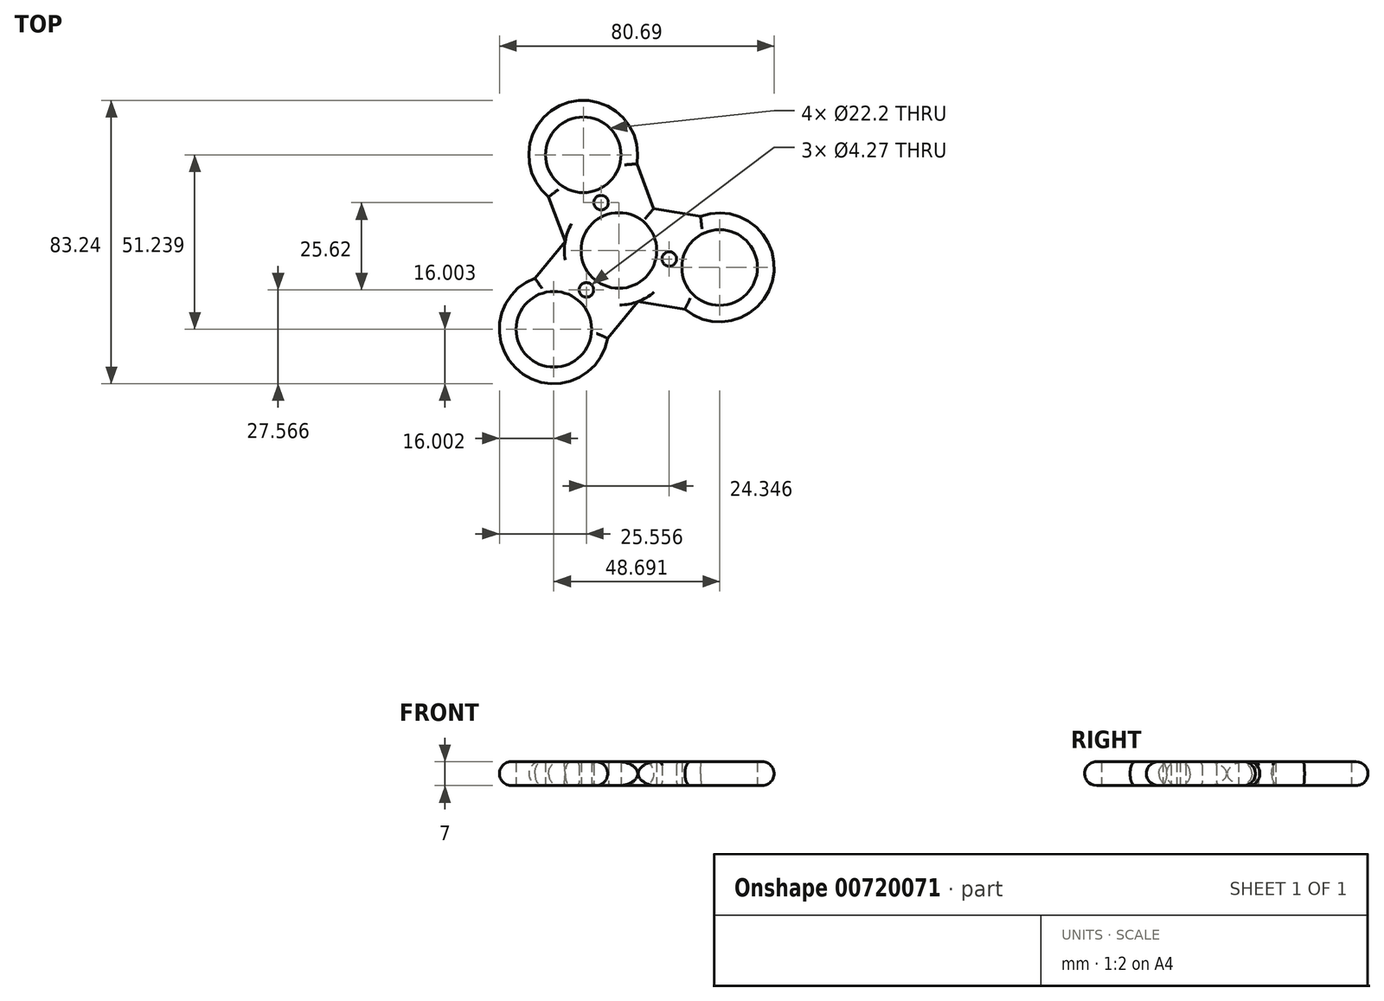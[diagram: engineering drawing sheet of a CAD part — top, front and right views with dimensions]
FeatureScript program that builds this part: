
annotation { "Feature Type Name" : "Feature", "Feature Type Description" : "" }
export const myFeature = defineFeature(function(context is Context, id is Id, definition is map)
    precondition{}
    {
        {
            var Q0;
            Q0=qCreatedBy(makeId("Top.planeOp"),FACE);
            var sketch = newSketch(context, id + "F0", { "sketchPlane" : qUnion([Q0])});
            skCircle(sketch, "E0", {"center": v(0, 0) * mm, "radius": 11.1 * mm});
            skLineSegment(sketch, "E1", {"start": v(0, 0) * mm, "end": v(-10.47, 28.11) * mm});
            skLineSegment(sketch, "E2", {"start": v(0, 0) * mm, "end": v(-19.1, -23.13) * mm});
            skLineSegment(sketch, "E3", {"start": v(0, 0) * mm, "end": v(29.58, -4.98) * mm});
            skCircle(sketch, "E4", {"center": v(-10.47, 28.11) * mm, "radius": 11.1 * mm});
            skCircle(sketch, "E5", {"center": v(29.58, -4.98) * mm, "radius": 11.1 * mm});
            skCircle(sketch, "E6", {"center": v(-19.1, -23.13) * mm, "radius": 11.1 * mm});
            skCircle(sketch, "E7", {"center": v(-10.47, 28.11) * mm, "radius": 16 * mm});
            skCircle(sketch, "E8", {"center": v(29.58, -4.98) * mm, "radius": 16 * mm});
            skCircle(sketch, "E9", {"center": v(-19.1, -23.13) * mm, "radius": 16 * mm});
            skCircle(sketch, "E10", {"center": v(0, 0) * mm, "radius": 16 * mm});
            skLineSegment(sketch, "E11", {"start": v(0, 0) * mm, "end": v(-15.77, 2.7) * mm, "construction": true});
            skLineSegment(sketch, "E12", {"start": v(0, 0) * mm, "end": v(10.2, 12.33) * mm, "construction": true});
            skLineSegment(sketch, "E13", {"start": v(-10.47, 28.11) * mm, "end": v(-20.67, 15.78) * mm, "construction": true});
            skLineSegment(sketch, "E14", {"start": v(-10.47, 28.11) * mm, "end": v(5.3, 25.45) * mm});
            skLineSegment(sketch, "E15", {"start": v(10.2, 12.33) * mm, "end": v(5.3, 25.45) * mm});
            skLineSegment(sketch, "E16", {"start": v(-15.77, 2.7) * mm, "end": v(-20.67, 15.78) * mm});
            skLineSegment(sketch, "E17.MirrorCS", {"start": v(5.63, -14.98) * mm, "end": v(19.4, -17.32) * mm});
            skLineSegment(sketch, "E18.MirrorCS", {"start": v(10.2, 12.33) * mm, "end": v(24, 10) * mm});
            skLineSegment(sketch, "E19.MirrorCS", {"start": v(-15.79, 2.6) * mm, "end": v(-24.7, -8.13) * mm});
            skLineSegment(sketch, "E20.MirrorCS", {"start": v(5.59, -15) * mm, "end": v(-3.33, -25.79) * mm});
            skLineSegment(sketch, "E21", {"start": v(-3.88, 10.4) * mm, "end": v(-6.6, 17.71) * mm});
            skLineSegment(sketch, "E22", {"start": v(-3.88, 10.4) * mm, "end": v(-5.24, 14.06) * mm});
            skCircle(sketch, "E23", {"center": v(-5.24, 14.06) * mm, "radius": 2.14 * mm});
            skCircle(sketch, "E24.MirrorC", {"center": v(-9.55, -11.56) * mm, "radius": 2.14 * mm});
            skCircle(sketch, "E25.MirrorC", {"center": v(14.8, -2.5) * mm, "radius": 2.14 * mm});
            skSolve(sketch);
        }
        {
            var Q0;
            Q0=makeQuery(id+"F0.imprint","IMPRINT",FACE,{"disambiguationData":[TD([[makeQuery(id+"F0.imprint","IMPRINT",EDGE,{"derivedFrom":sQuery(id+"F0.wireOp",EDGE,"E5")}),-1.0]])]});
            var Q1;
            Q1=makeQuery(id+"F0.imprint","IMPRINT",FACE,{"disambiguationData":[TD([[makeQuery(id+"F0.imprint","IMPRINT",EDGE,{"derivedFrom":sQuery(id+"F0.wireOp",EDGE,"E6")}),-1.0]])]});
            var Q2;
            {var subQ4=sQuery(id+"F0.wireOp",EDGE,"E2");var subQ5=sQuery(id+"F0.wireOp",EDGE,"E0");var subQ6=makeQuery(id+"F0.imprint","INTERSECT",VERTEX,{"derivedFrom":[subQ5,subQ4]});Q2=makeQuery(id+"F0.imprint","IMPRINT",FACE,{"disambiguationData":[TD([[makeQuery(id+"F0.imprint","IMPRINT",EDGE,{"disambiguationData":[TD([[subQ6,1.0]])],"derivedFrom":subQ5}),-1.0]])]});}
            var Q3;
            {var subQ2=sQuery(id+"F0.wireOp",EDGE,"E2");var subQ5=sQuery(id+"F0.wireOp",EDGE,"E0");var subQ8=makeQuery(id+"F0.imprint","INTERSECT",VERTEX,{"derivedFrom":[subQ5,subQ2]});Q3=makeQuery(id+"F0.imprint","IMPRINT",FACE,{"disambiguationData":[TD([[makeQuery(id+"F0.imprint","IMPRINT",EDGE,{"disambiguationData":[TD([[subQ8,-1.0]])],"derivedFrom":subQ5}),-1.0]])]});}
            var Q4;
            {var subQ0=sQuery(id+"F0.wireOp",EDGE,"E1");var subQ1=sQuery(id+"F0.wireOp",EDGE,"E0");var subQ2=makeQuery(id+"F0.imprint","INTERSECT",VERTEX,{"derivedFrom":[subQ1,subQ0]});Q4=makeQuery(id+"F0.imprint","IMPRINT",FACE,{"disambiguationData":[TD([[makeQuery(id+"F0.imprint","IMPRINT",EDGE,{"disambiguationData":[TD([[subQ2,1.0]])],"derivedFrom":subQ1}),-1.0]])]});}
            var Q5;
            {var subQ0=sQuery(id+"F0.wireOp",EDGE,"wNWGQW3L-Wg3f-4ug6-IvEM-VYyaZqjxjgMl");var subQ1=sQuery(id+"F0.wireOp",EDGE,"E20.MirrorCS");var subQ2=makeQuery(id+"F0.imprint","INTERSECT",VERTEX,{"disambiguationData":[OD(0.0)],"derivedFrom":[subQ1,subQ0]});Q5=makeQuery(id+"F0.imprint","IMPRINT",FACE,{"disambiguationData":[TD([[makeQuery(id+"F0.imprint","IMPRINT",EDGE,{"disambiguationData":[TD([[subQ2,-1.0]])],"derivedFrom":subQ1}),1.0]])]});}
            var Q6;
            {var subQ0=sQuery(id+"F0.wireOp",EDGE,"StkbR3Lz-Og8J-Unaf-IOIf-LEIyfNda2m4F");var subQ1=sQuery(id+"F0.wireOp",EDGE,"E9");var subQ2=makeQuery(id+"F0.imprint","INTERSECT",VERTEX,{"disambiguationData":[OD(0.0)],"derivedFrom":[subQ1,subQ0]});Q6=makeQuery(id+"F0.imprint","IMPRINT",FACE,{"disambiguationData":[TD([[makeQuery(id+"F0.imprint","IMPRINT",EDGE,{"disambiguationData":[TD([[subQ2,1.0]])],"derivedFrom":subQ1}),1.0]])]});}
            var Q7;
            {var subQ0=sQuery(id+"F0.wireOp",EDGE,"StkbR3Lz-Og8J-Unaf-IOIf-LEIyfNda2m4F");var subQ1=sQuery(id+"F0.wireOp",EDGE,"E9");var subQ2=makeQuery(id+"F0.imprint","INTERSECT",VERTEX,{"disambiguationData":[OD(1.0)],"derivedFrom":[subQ1,subQ0]});Q7=makeQuery(id+"F0.imprint","IMPRINT",FACE,{"disambiguationData":[TD([[makeQuery(id+"F0.imprint","IMPRINT",EDGE,{"disambiguationData":[TD([[subQ2,-1.0]])],"derivedFrom":subQ1}),1.0]])]});}
            var Q8;
            {var subQ0=sQuery(id+"F0.wireOp",EDGE,"E10");var subQ1=sQuery(id+"F0.wireOp",EDGE,"E8");var subQ2=makeQuery(id+"F0.imprint","INTERSECT",VERTEX,{"disambiguationData":[OD(0.0)],"derivedFrom":[subQ1,subQ0]});Q8=makeQuery(id+"F0.imprint","IMPRINT",FACE,{"disambiguationData":[TD([[makeQuery(id+"F0.imprint","IMPRINT",EDGE,{"disambiguationData":[TD([[subQ2,-1.0]])],"derivedFrom":subQ1}),1.0]])]});}
            var Q9;
            {var subQ0=sQuery(id+"F0.wireOp",EDGE,"1e5d11e3-8aaf-4e84-b3b0-f10da001fed20.MirrorC");var subQ1=sQuery(id+"F0.wireOp",EDGE,"E8");var subQ2=makeQuery(id+"F0.imprint","INTERSECT",VERTEX,{"disambiguationData":[OD(1.0)],"derivedFrom":[subQ1,subQ0]});Q9=makeQuery(id+"F0.imprint","IMPRINT",FACE,{"disambiguationData":[TD([[makeQuery(id+"F0.imprint","IMPRINT",EDGE,{"disambiguationData":[TD([[subQ2,-1.0]])],"derivedFrom":subQ1}),1.0]])]});}
            var Q10;
            {var subQ3=sQuery(id+"F0.wireOp",EDGE,"171ab229-298c-4372-97cf-4ced48a297110.MirrorC");var subQ8=sQuery(id+"F0.wireOp",EDGE,"E1");var subQ11=makeQuery(id+"F0.imprint","INTERSECT",VERTEX,{"disambiguationData":[OD(1.0)],"derivedFrom":[subQ8,subQ3]});Q10=makeQuery(id+"F0.imprint","IMPRINT",FACE,{"disambiguationData":[TD([[makeQuery(id+"F0.imprint","IMPRINT",EDGE,{"disambiguationData":[TD([[subQ11,-1.0]])],"derivedFrom":subQ8}),-1.0]])]});}
            var Q11;
            {var subQ4=sQuery(id+"F0.wireOp",EDGE,"171ab229-298c-4372-97cf-4ced48a297110.MirrorC");var subQ5=sQuery(id+"F0.wireOp",EDGE,"E1");var subQ6=makeQuery(id+"F0.imprint","INTERSECT",VERTEX,{"disambiguationData":[OD(1.0)],"derivedFrom":[subQ5,subQ4]});Q11=makeQuery(id+"F0.imprint","IMPRINT",FACE,{"disambiguationData":[TD([[makeQuery(id+"F0.imprint","IMPRINT",EDGE,{"disambiguationData":[TD([[subQ6,-1.0]])],"derivedFrom":subQ5}),1.0]])]});}
            var Q12;
            {var subQ0=sQuery(id+"F0.wireOp",EDGE,"171ab229-298c-4372-97cf-4ced48a297110.MirrorC");var subQ1=sQuery(id+"F0.wireOp",EDGE,"E7");var subQ2=makeQuery(id+"F0.imprint","INTERSECT",VERTEX,{"disambiguationData":[OD(1.0)],"derivedFrom":[subQ1,subQ0]});Q12=makeQuery(id+"F0.imprint","IMPRINT",FACE,{"disambiguationData":[TD([[makeQuery(id+"F0.imprint","IMPRINT",EDGE,{"disambiguationData":[TD([[subQ2,-1.0]])],"derivedFrom":subQ1}),1.0]])]});}
            var Q13;
            {var subQ0=sQuery(id+"F0.wireOp",EDGE,"E10");var subQ1=sQuery(id+"F0.wireOp",EDGE,"E7");var subQ2=makeQuery(id+"F0.imprint","INTERSECT",VERTEX,{"disambiguationData":[OD(0.0)],"derivedFrom":[subQ1,subQ0]});Q13=makeQuery(id+"F0.imprint","IMPRINT",FACE,{"disambiguationData":[TD([[makeQuery(id+"F0.imprint","IMPRINT",EDGE,{"disambiguationData":[TD([[subQ2,-1.0]])],"derivedFrom":subQ1}),1.0]])]});}
            var Q14;
            {var subQ1=sQuery(id+"F0.wireOp",EDGE,"e612f9c1-c014-4065-8786-90dc7a8c4ea60.MirrorCS");Q14=makeQuery(id+"F0.imprint","IMPRINT",FACE,{"disambiguationData":[TD([[makeQuery(id+"F0.imprint","IMPRINT",EDGE,{"derivedFrom":subQ1}),1.0]])]});}
            var Q15;
            {var subQ5=sQuery(id+"F0.wireOp",EDGE,"E14");var subQ7=sQuery(id+"F0.wireOp",EDGE,"E4");var subQ8=makeQuery(id+"F0.imprint","INTERSECT",VERTEX,{"derivedFrom":[subQ7,subQ5]});Q15=makeQuery(id+"F0.imprint","IMPRINT",FACE,{"disambiguationData":[TD([[makeQuery(id+"F0.imprint","IMPRINT",EDGE,{"disambiguationData":[TD([[subQ8,1.0]])],"derivedFrom":subQ7}),-1.0]])]});}
            var Q16;
            {var subQ5=sQuery(id+"F0.wireOp",EDGE,"E14");var subQ9=sQuery(id+"F0.wireOp",EDGE,"E4");var subQ12=makeQuery(id+"F0.imprint","INTERSECT",VERTEX,{"derivedFrom":[subQ9,subQ5]});Q16=makeQuery(id+"F0.imprint","IMPRINT",FACE,{"disambiguationData":[TD([[makeQuery(id+"F0.imprint","IMPRINT",EDGE,{"disambiguationData":[TD([[subQ12,-1.0]])],"derivedFrom":subQ9}),-1.0]])]});}
            var Q17;
            {var subQ0=sQuery(id+"F0.wireOp",EDGE,"32d44365-9099-444c-8909-6f45dbab55cc0.MirrorCS");Q17=makeQuery(id+"F0.imprint","IMPRINT",FACE,{"disambiguationData":[TD([[makeQuery(id+"F0.imprint","IMPRINT",EDGE,{"derivedFrom":subQ0}),-1.0]])]});}
            var Q18;
            {var subQ0=sQuery(id+"F0.wireOp",EDGE,"ae01513f-205a-4772-8993-a33fd46c5e690.MirrorCS");Q18=makeQuery(id+"F0.imprint","IMPRINT",FACE,{"disambiguationData":[TD([[makeQuery(id+"F0.imprint","IMPRINT",EDGE,{"derivedFrom":subQ0}),1.0]])]});}
            var Q19;
            {var subQ0=sQuery(id+"F0.wireOp",EDGE,"c8ff0e85-610d-4f0e-9ecb-1ba7e22bc6e30.MirrorCS");Q19=makeQuery(id+"F0.imprint","IMPRINT",FACE,{"disambiguationData":[TD([[makeQuery(id+"F0.imprint","IMPRINT",EDGE,{"derivedFrom":subQ0}),-1.0]])]});}
            var Q20;
            {var subQ1=sQuery(id+"F0.wireOp",EDGE,"91903ac2-48b2-40ea-bbcb-57abc5b5aab90.MirrorCS");Q20=makeQuery(id+"F0.imprint","IMPRINT",FACE,{"disambiguationData":[TD([[makeQuery(id+"F0.imprint","IMPRINT",EDGE,{"derivedFrom":subQ1}),-1.0]])]});}
            var Q21;
            {var subQ0=sQuery(id+"F0.wireOp",EDGE,"8dce575f-2467-473e-b586-ea05cfbc66d80.MirrorCS");Q21=makeQuery(id+"F0.imprint","IMPRINT",FACE,{"disambiguationData":[TD([[makeQuery(id+"F0.imprint","IMPRINT",EDGE,{"derivedFrom":subQ0}),1.0]])]});}
            var Q22;
            {var subQ0=sQuery(id+"F0.wireOp",EDGE,"E24.MirrorC");var subQ1=sQuery(id+"F0.wireOp",EDGE,"E9");var subQ2=makeQuery(id+"F0.imprint","INTERSECT",VERTEX,{"disambiguationData":[OD(1.0)],"derivedFrom":[subQ1,subQ0]});Q22=makeQuery(id+"F0.imprint","IMPRINT",FACE,{"disambiguationData":[TD([[makeQuery(id+"F0.imprint","IMPRINT",EDGE,{"disambiguationData":[TD([[subQ2,-1.0]])],"derivedFrom":subQ1}),1.0]])]});}
            var Q23;
            {var subQ0=sQuery(id+"F0.wireOp",EDGE,"E24.MirrorC");var subQ1=sQuery(id+"F0.wireOp",EDGE,"E9");var subQ2=makeQuery(id+"F0.imprint","INTERSECT",VERTEX,{"disambiguationData":[OD(0.0)],"derivedFrom":[subQ1,subQ0]});Q23=makeQuery(id+"F0.imprint","IMPRINT",FACE,{"disambiguationData":[TD([[makeQuery(id+"F0.imprint","IMPRINT",EDGE,{"disambiguationData":[TD([[subQ2,1.0]])],"derivedFrom":subQ1}),1.0]])]});}
            var Q24;
            {var subQ0=sQuery(id+"F0.wireOp",EDGE,"E25.MirrorC");var subQ1=sQuery(id+"F0.wireOp",EDGE,"E8");var subQ2=makeQuery(id+"F0.imprint","INTERSECT",VERTEX,{"disambiguationData":[OD(1.0)],"derivedFrom":[subQ1,subQ0]});Q24=makeQuery(id+"F0.imprint","IMPRINT",FACE,{"disambiguationData":[TD([[makeQuery(id+"F0.imprint","IMPRINT",EDGE,{"disambiguationData":[TD([[subQ2,-1.0]])],"derivedFrom":subQ1}),1.0]])]});}
            var Q25;
            {var subQ0=sQuery(id+"F0.wireOp",EDGE,"E23");var subQ1=sQuery(id+"F0.wireOp",EDGE,"E7");var subQ2=makeQuery(id+"F0.imprint","INTERSECT",VERTEX,{"disambiguationData":[OD(1.0)],"derivedFrom":[subQ1,subQ0]});Q25=makeQuery(id+"F0.imprint","IMPRINT",FACE,{"disambiguationData":[TD([[makeQuery(id+"F0.imprint","IMPRINT",EDGE,{"disambiguationData":[TD([[subQ2,-1.0]])],"derivedFrom":subQ1}),1.0]])]});}
            var Q26;
            {var subQ0=sQuery(id+"F0.wireOp",EDGE,"E20.MirrorCS");Q26=makeQuery(id+"F0.imprint","IMPRINT",FACE,{"disambiguationData":[TD([[makeQuery(id+"F0.imprint","IMPRINT",EDGE,{"derivedFrom":subQ0}),-1.0]])]});}
            var Q27;
            {var subQ0=sQuery(id+"F0.wireOp",EDGE,"E17.MirrorCS");Q27=makeQuery(id+"F0.imprint","IMPRINT",FACE,{"disambiguationData":[TD([[makeQuery(id+"F0.imprint","IMPRINT",EDGE,{"derivedFrom":subQ0}),1.0]])]});}
            var Q28;
            {var subQ0=sQuery(id+"F0.wireOp",EDGE,"E19.MirrorCS");Q28=makeQuery(id+"F0.imprint","IMPRINT",FACE,{"disambiguationData":[TD([[makeQuery(id+"F0.imprint","IMPRINT",EDGE,{"derivedFrom":subQ0}),1.0]])]});}
            var Q29;
            {var subQ0=sQuery(id+"F0.wireOp",EDGE,"E16");Q29=makeQuery(id+"F0.imprint","IMPRINT",FACE,{"disambiguationData":[TD([[makeQuery(id+"F0.imprint","IMPRINT",EDGE,{"derivedFrom":subQ0}),-1.0]])]});}
            var Q30;
            {var subQ0=sQuery(id+"F0.wireOp",EDGE,"E15");Q30=makeQuery(id+"F0.imprint","IMPRINT",FACE,{"disambiguationData":[TD([[makeQuery(id+"F0.imprint","IMPRINT",EDGE,{"derivedFrom":subQ0}),1.0]])]});}
            var Q31;
            {var subQ0=sQuery(id+"F0.wireOp",EDGE,"E18.MirrorCS");Q31=makeQuery(id+"F0.imprint","IMPRINT",FACE,{"disambiguationData":[TD([[makeQuery(id+"F0.imprint","IMPRINT",EDGE,{"derivedFrom":subQ0}),-1.0]])]});}
            extrude(context, id + "F1", {"entities" : qUnion([Q0, Q1, Q2, Q3, Q4, Q5, Q6, Q7, Q8, Q9, Q10, Q11, Q12, Q13, Q14, Q15, Q16, Q17, Q18, Q19, Q20, Q21, Q22, Q23, Q24, Q25, Q26, Q27, Q28, Q29, Q30, Q31]), "depth" : 7 * mm, "offsetDistance" : 25 * mm});
        }
        {
            var Q0;
            Q0=makeQuery(id+"F1.opExtrude","CAP_EDGE",EDGE,{"disambiguationData":[OSD([sQuery(id+"F0.wireOp",EDGE,"StkbR3Lz-Og8J-Unaf-IOIf-LEIyfNda2m4F")])],"isStart":false});
            var Q1;
            Q1=makeQuery(id+"F1.opExtrude","CAP_EDGE",EDGE,{"disambiguationData":[OSD([sQuery(id+"F0.wireOp",EDGE,"1e5d11e3-8aaf-4e84-b3b0-f10da001fed20.MirrorC")])],"isStart":false});
            var Q2;
            Q2=makeQuery(id+"F1.opExtrude","CAP_EDGE",EDGE,{"disambiguationData":[OSD([sQuery(id+"F0.wireOp",EDGE,"171ab229-298c-4372-97cf-4ced48a297110.MirrorC")])],"isStart":false});
            var Q3;
            Q3=makeQuery(id+"F1.opExtrude","CAP_EDGE",EDGE,{"disambiguationData":[OSD([sQuery(id+"F0.wireOp",EDGE,"E24.MirrorC")])],"isStart":true});
            var Q4;
            Q4=makeQuery(id+"F1.opExtrude","CAP_EDGE",EDGE,{"disambiguationData":[OSD([sQuery(id+"F0.wireOp",EDGE,"E23")])],"isStart":true});
            var Q5;
            Q5=makeQuery(id+"F1.opExtrude","CAP_EDGE",EDGE,{"disambiguationData":[OSD([sQuery(id+"F0.wireOp",EDGE,"E25.MirrorC")])],"isStart":true});
            var Q6;
            Q6=makeQuery(id+"F1.opExtrude","CAP_EDGE",EDGE,{"disambiguationData":[OSD([sQuery(id+"F0.wireOp",EDGE,"E25.MirrorC")])],"isStart":false});
            var Q7;
            Q7=makeQuery(id+"F1.opExtrude","CAP_EDGE",EDGE,{"disambiguationData":[OSD([sQuery(id+"F0.wireOp",EDGE,"E23")])],"isStart":false});
            var Q8;
            Q8=makeQuery(id+"F1.opExtrude","CAP_EDGE",EDGE,{"disambiguationData":[OSD([sQuery(id+"F0.wireOp",EDGE,"E24.MirrorC")])],"isStart":false});
            fillet(context, id + "F2", {"entities" : qUnion([Q0, Q1, Q2, Q3, Q4, Q5, Q6, Q7, Q8]), "radius" : 1 * mm, "tangentPropagation" : true, "allowEdgeOverflow" : false});
        }
        {
            var Q0;
            Q0=makeQuery(id+"F1.opExtrude","CAP_EDGE",EDGE,{"disambiguationData":[OSD([sQuery(id+"F0.wireOp",EDGE,"E9")])],"isStart":true});
            var Q1;
            Q1=makeQuery(id+"F1.opExtrude","CAP_EDGE",EDGE,{"disambiguationData":[OSD([sQuery(id+"F0.wireOp",EDGE,"E19.MirrorCS")])],"isStart":true});
            var Q2;
            Q2=makeQuery(id+"F1.opExtrude","CAP_EDGE",EDGE,{"disambiguationData":[OSD([sQuery(id+"F0.wireOp",EDGE,"E20.MirrorCS")])],"isStart":true});
            var Q3;
            Q3=makeQuery(id+"F1.opExtrude","CAP_EDGE",EDGE,{"disambiguationData":[OSD([sQuery(id+"F0.wireOp",EDGE,"E17.MirrorCS")])],"isStart":true});
            var Q4;
            Q4=makeQuery(id+"F1.opExtrude","CAP_EDGE",EDGE,{"disambiguationData":[OSD([sQuery(id+"F0.wireOp",EDGE,"E8")])],"isStart":true});
            var Q5;
            Q5=makeQuery(id+"F1.opExtrude","CAP_EDGE",EDGE,{"disambiguationData":[OSD([sQuery(id+"F0.wireOp",EDGE,"E18.MirrorCS")])],"isStart":true});
            var Q6;
            Q6=makeQuery(id+"F1.opExtrude","CAP_EDGE",EDGE,{"disambiguationData":[OSD([sQuery(id+"F0.wireOp",EDGE,"E15")])],"isStart":true});
            var Q7;
            Q7=makeQuery(id+"F1.opExtrude","CAP_EDGE",EDGE,{"disambiguationData":[OSD([sQuery(id+"F0.wireOp",EDGE,"E16")])],"isStart":true});
            var Q8;
            Q8=makeQuery(id+"F1.opExtrude","CAP_EDGE",EDGE,{"disambiguationData":[OSD([sQuery(id+"F0.wireOp",EDGE,"E7")])],"isStart":true});
            var Q9;
            Q9=makeQuery(id+"F1.opExtrude","CAP_EDGE",EDGE,{"disambiguationData":[OSD([sQuery(id+"F0.wireOp",EDGE,"E9")])],"isStart":false});
            var Q10;
            Q10=makeQuery(id+"F1.opExtrude","CAP_EDGE",EDGE,{"disambiguationData":[OSD([sQuery(id+"F0.wireOp",EDGE,"E19.MirrorCS")])],"isStart":false});
            var Q11;
            Q11=makeQuery(id+"F1.opExtrude","CAP_EDGE",EDGE,{"disambiguationData":[OSD([sQuery(id+"F0.wireOp",EDGE,"E20.MirrorCS")])],"isStart":false});
            var Q12;
            Q12=makeQuery(id+"F1.opExtrude","CAP_EDGE",EDGE,{"disambiguationData":[OSD([sQuery(id+"F0.wireOp",EDGE,"E17.MirrorCS")])],"isStart":false});
            var Q13;
            Q13=makeQuery(id+"F1.opExtrude","CAP_EDGE",EDGE,{"disambiguationData":[OSD([sQuery(id+"F0.wireOp",EDGE,"E18.MirrorCS")])],"isStart":false});
            var Q14;
            Q14=makeQuery(id+"F1.opExtrude","CAP_EDGE",EDGE,{"disambiguationData":[OSD([sQuery(id+"F0.wireOp",EDGE,"E8")])],"isStart":false});
            var Q15;
            Q15=makeQuery(id+"F1.opExtrude","CAP_EDGE",EDGE,{"disambiguationData":[OSD([sQuery(id+"F0.wireOp",EDGE,"E15")])],"isStart":false});
            var Q16;
            Q16=makeQuery(id+"F1.opExtrude","CAP_EDGE",EDGE,{"disambiguationData":[OSD([sQuery(id+"F0.wireOp",EDGE,"E16")])],"isStart":false});
            var Q17;
            Q17=makeQuery(id+"F1.opExtrude","CAP_EDGE",EDGE,{"disambiguationData":[OSD([sQuery(id+"F0.wireOp",EDGE,"E7")])],"isStart":false});
            var Q18;
            Q18=makeQuery(id+"F1.opExtrude","CAP_EDGE",EDGE,{"disambiguationData":[OSD([sQuery(id+"F0.wireOp",EDGE,"e612f9c1-c014-4065-8786-90dc7a8c4ea60.MirrorCS")])],"isStart":false});
            var Q19;
            Q19=makeQuery(id+"F1.opExtrude","CAP_EDGE",EDGE,{"disambiguationData":[OSD([sQuery(id+"F0.wireOp",EDGE,"c8ff0e85-610d-4f0e-9ecb-1ba7e22bc6e30.MirrorCS")])],"isStart":false});
            var Q20;
            Q20=makeQuery(id+"F1.opExtrude","CAP_EDGE",EDGE,{"disambiguationData":[OSD([sQuery(id+"F0.wireOp",EDGE,"32d44365-9099-444c-8909-6f45dbab55cc0.MirrorCS")])],"isStart":false});
            var Q21;
            Q21=makeQuery(id+"F1.opExtrude","CAP_EDGE",EDGE,{"disambiguationData":[OSD([sQuery(id+"F0.wireOp",EDGE,"ae01513f-205a-4772-8993-a33fd46c5e690.MirrorCS")])],"isStart":false});
            fillet(context, id + "F3", {"entities" : qUnion([Q0, Q1, Q2, Q3, Q4, Q5, Q6, Q7, Q8, Q9, Q10, Q11, Q12, Q13, Q14, Q15, Q16, Q17, Q18, Q19, Q20, Q21]), "radius" : 3.5 * mm, "tangentPropagation" : true, "allowEdgeOverflow" : false});
        }
    });
